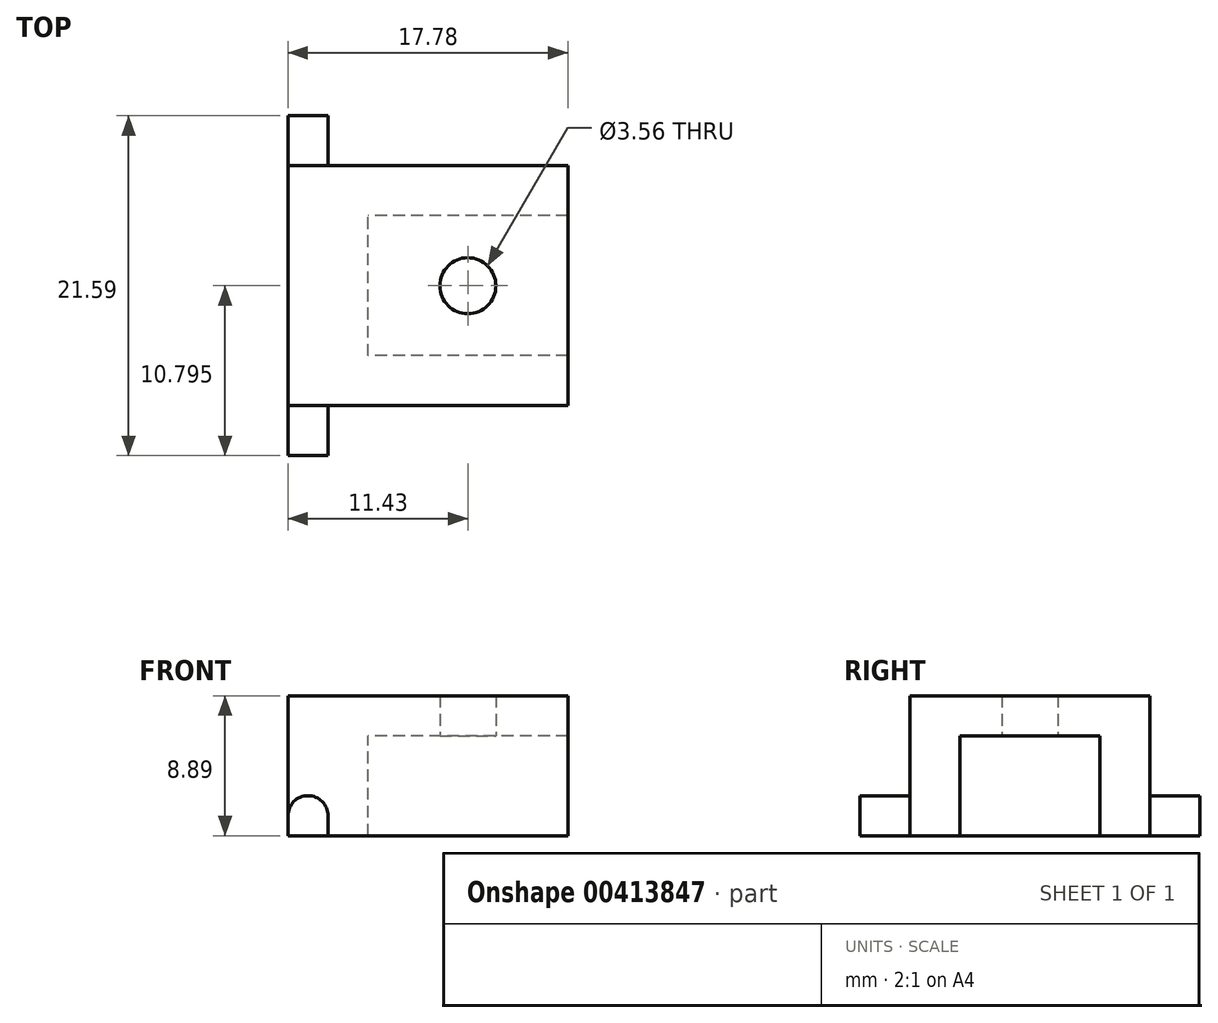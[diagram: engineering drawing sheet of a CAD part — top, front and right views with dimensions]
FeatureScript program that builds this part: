
annotation { "Feature Type Name" : "Feature", "Feature Type Description" : "" }
export const myFeature = defineFeature(function(context is Context, id is Id, definition is map)
    precondition{}
    {
        {
            var Q0;
            Q0=qCreatedBy(makeId("Front.planeOp"),FACE);
            var sketch = newSketch(context, id + "F0", { "sketchPlane" : qUnion([Q0])});
            skLineSegment(sketch, "E0.bottom", {"start": v(0, 0) * mm, "end": v(2.54, 0) * mm});
            skLineSegment(sketch, "E0.top", {"start": v(0, 2.54) * mm, "end": v(2.54, 2.54) * mm});
            skLineSegment(sketch, "E0.left", {"start": v(0, 0) * mm, "end": v(0, 2.54) * mm});
            skLineSegment(sketch, "E0.right", {"start": v(2.54, 0) * mm, "end": v(2.54, 2.54) * mm});
            skSolve(sketch);
        }
        {
            var Q0;
            Q0 = qSketchRegion(id + "F0", true);
            extrude(context, id + "F1", {"entities" : qUnion([Q0]), "depth" : 21.59 * mm});
        }
        {
            var Q0;
            Q0=makeQuery(id+"F1.opExtrude","SWEPT_FACE",FACE,{"disambiguationData":[OSD([sQuery(id+"F0.wireOp",EDGE,"E0.right")])]});
            var sketch = newSketch(context, id + "F2", { "sketchPlane" : qUnion([Q0])});
            skLineSegment(sketch, "E1", {"start": v(-21.59, 2.54) * mm, "end": v(-18.41, 2.54) * mm});
            skLineSegment(sketch, "E2", {"start": v(-18.41, 2.54) * mm, "end": v(-18.41, 8.9) * mm});
            skLineSegment(sketch, "E3", {"start": v(-18.41, 8.9) * mm, "end": v(-3.18, 8.9) * mm});
            skLineSegment(sketch, "E4", {"start": v(-3.18, 8.9) * mm, "end": v(-3.18, 2.54) * mm});
            skLineSegment(sketch, "E5", {"start": v(-3.18, 2.54) * mm, "end": v(0, 2.54) * mm});
            skLineSegment(sketch, "E6", {"start": v(-18.41, 2.54) * mm, "end": v(-18.41, 0) * mm});
            skLineSegment(sketch, "E7", {"start": v(-18.41, 0) * mm, "end": v(-3.18, 0) * mm});
            skLineSegment(sketch, "E8", {"start": v(-3.18, 0) * mm, "end": v(-3.18, 2.54) * mm});
            skSolve(sketch);
        }
        {
            var Q0;
            Q0 = qSketchRegion(id + "F2", true);
            var Q1;
            Q1=makeQuery(id+"F1.opExtrude","SWEPT_FACE",FACE,{"disambiguationData":[OSD([sQuery(id+"F0.wireOp",EDGE,"E0.left")])]});
            extrude(context, id + "F3", {"entities" : qUnion([Q0]), "operationType" : NewBodyOperationType.ADD, "depth" : 2.54 * mm, "hasSecondDirection" : true, "secondDirectionBound" : SecondDirectionBoundingType.UP_TO_SURFACE, "secondDirectionOppositeDirection" : true, "secondDirectionBoundEntityFace" : qUnion([Q1]), "secondDirectionDepth" : 25.4 * mm});
        }
        {
            var Q0;
            Q0=makeQuery(id+"F3.opExtrude","CAP_FACE",FACE,{"disambiguationData":[OSD([sQuery(id+"F2.wireOp",EDGE,"E2"),sQuery(id+"F2.wireOp",EDGE,"E3"),sQuery(id+"F2.wireOp",EDGE,"E4"),sQuery(id+"F2.wireOp",EDGE,"E6"),sQuery(id+"F2.wireOp",EDGE,"E7"),sQuery(id+"F2.wireOp",EDGE,"E8")])],"isStart":false});
            var sketch = newSketch(context, id + "F4", { "sketchPlane" : qUnion([Q0])});
            skLineSegment(sketch, "E9", {"start": v(-18.41, 0) * mm, "end": v(-18.41, 8.9) * mm});
            skLineSegment(sketch, "E10", {"start": v(-18.41, 8.9) * mm, "end": v(-3.18, 8.9) * mm});
            skLineSegment(sketch, "E11", {"start": v(-3.18, 8.9) * mm, "end": v(-3.18, 0) * mm});
            skLineSegment(sketch, "E12", {"start": v(-3.18, 0) * mm, "end": v(-6.35, 0) * mm});
            skLineSegment(sketch, "E13", {"start": v(-6.35, 0) * mm, "end": v(-6.35, 6.35) * mm});
            skLineSegment(sketch, "E14", {"start": v(-6.35, 6.35) * mm, "end": v(-15.24, 6.35) * mm});
            skLineSegment(sketch, "E15", {"start": v(-15.24, 6.35) * mm, "end": v(-15.24, 0) * mm});
            skLineSegment(sketch, "E16", {"start": v(-15.24, 0) * mm, "end": v(-18.41, 0) * mm});
            skSolve(sketch);
        }
        {
            var Q0;
            Q0 = qSketchRegion(id + "F4", true);
            extrude(context, id + "F5", {"entities" : qUnion([Q0]), "operationType" : NewBodyOperationType.ADD, "depth" : 12.7 * mm});
        }
        {
            var Q0;
            Q0=makeQuery(id+"F5.opExtrude","SWEPT_FACE",FACE,{"disambiguationData":[OSD([sQuery(id+"F4.wireOp",EDGE,"E14")])]});
            var sketch = newSketch(context, id + "F6", { "sketchPlane" : qUnion([Q0])});
            skLineSegment(sketch, "E17", {"start": v(5.08, 6.35) * mm, "end": v(17.78, 15.24) * mm});
            skCircle(sketch, "E18", {"center": v(11.43, 10.8) * mm, "radius": 1.78 * mm});
            skSolve(sketch);
        }
        {
            var Q0;
            Q0 = qSketchRegion(id + "F6", true);
            extrude(context, id + "F7", {"entities" : qUnion([Q0]), "operationType" : NewBodyOperationType.REMOVE, "oppositeDirection" : true, "depth" : 25.4 * mm});
        }
        {
            var Q0;
            {var subQ0=sQuery(id+"F0.wireOp",EDGE,"E0.left");var subQ1=sQuery(id+"F0.wireOp",EDGE,"E0.top");Q0=makeQuery(id+"F3.boolean.opBoolean","SPLIT",EDGE,{"disambiguationData":[TD([makeQuery(id+"F3.opExtrude","SWEPT_FACE",FACE,{"disambiguationData":[OSD([sQuery(id+"F2.wireOp",EDGE,"E4"),sQuery(id+"F2.wireOp",EDGE,"E8")])]})])],"derivedFrom":makeQuery(id+"F1.opExtrude","SWEPT_EDGE",EDGE,{"disambiguationData":[OSD([subQ1,subQ0])]})});}
            var Q1;
            {var subQ0=sQuery(id+"F0.wireOp",EDGE,"E0.right");var subQ1=sQuery(id+"F0.wireOp",EDGE,"E0.top");Q1=makeQuery(id+"F3.boolean.opBoolean","SPLIT",EDGE,{"disambiguationData":[TD([makeQuery(id+"F3.opExtrude","SWEPT_FACE",FACE,{"disambiguationData":[OSD([sQuery(id+"F2.wireOp",EDGE,"E4"),sQuery(id+"F2.wireOp",EDGE,"E8")])]})])],"derivedFrom":makeQuery(id+"F1.opExtrude","SWEPT_EDGE",EDGE,{"disambiguationData":[OSD([subQ1,subQ0])]})});}
            var Q2;
            {var subQ0=sQuery(id+"F0.wireOp",EDGE,"E0.left");var subQ1=sQuery(id+"F0.wireOp",EDGE,"E0.top");Q2=makeQuery(id+"F3.boolean.opBoolean","SPLIT",EDGE,{"disambiguationData":[TD([makeQuery(id+"F3.opExtrude","SWEPT_FACE",FACE,{"disambiguationData":[OSD([sQuery(id+"F2.wireOp",EDGE,"E2"),sQuery(id+"F2.wireOp",EDGE,"E6")])]})])],"derivedFrom":makeQuery(id+"F1.opExtrude","SWEPT_EDGE",EDGE,{"disambiguationData":[OSD([subQ1,subQ0])]})});}
            var Q3;
            {var subQ0=sQuery(id+"F0.wireOp",EDGE,"E0.right");var subQ1=sQuery(id+"F0.wireOp",EDGE,"E0.top");Q3=makeQuery(id+"F3.boolean.opBoolean","SPLIT",EDGE,{"disambiguationData":[TD([makeQuery(id+"F3.opExtrude","SWEPT_FACE",FACE,{"disambiguationData":[OSD([sQuery(id+"F2.wireOp",EDGE,"E2"),sQuery(id+"F2.wireOp",EDGE,"E6")])]})])],"derivedFrom":makeQuery(id+"F1.opExtrude","SWEPT_EDGE",EDGE,{"disambiguationData":[OSD([subQ1,subQ0])]})});}
            fillet(context, id + "F8", {"entities" : qUnion([Q0, Q1, Q2, Q3]), "radius" : 1.27 * mm, "tangentPropagation" : true, "allowEdgeOverflow" : false});
        }
    });
